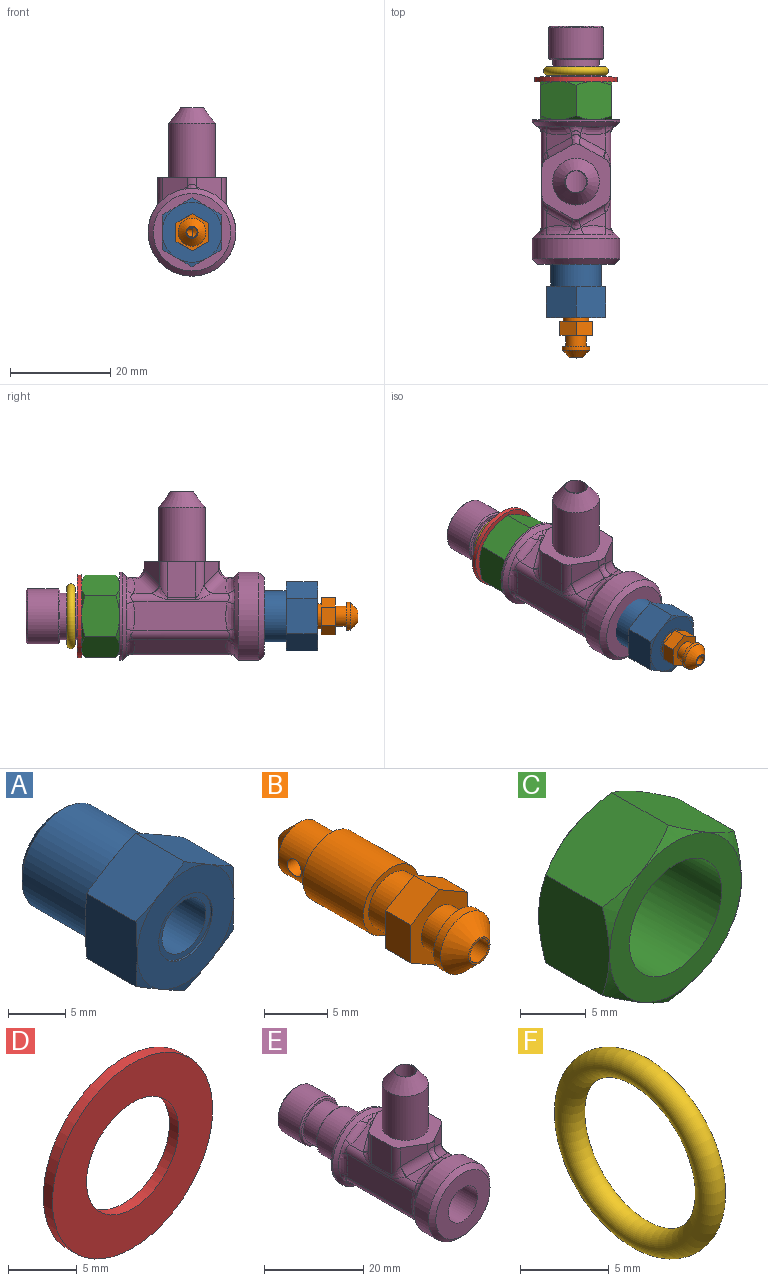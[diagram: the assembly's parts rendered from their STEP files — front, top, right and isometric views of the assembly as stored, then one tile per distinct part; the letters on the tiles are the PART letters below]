
ASSEMBLY  parts=6 mates=5
PART A: 29 faces, bbox 14.3x16.2x14.3 mm
  f0: cylinder r=2.71mm len=12.32mm, axis (0,-1,0), area 209.4mm2, adj f1,f26
  f1: cone r=0mm half-angle=59deg, axis (0,-1,0), area 21.7mm2, adj f0,f24
  f2: cylinder r=5.08mm len=10.16mm, axis (0,-1,0), area 278.1mm2, adj f4,f28
  f3: plane 8.89x8.89mm, normal (0,1,0), area 57.3mm2, adj f27,f28
  f4: plane 11.94x11.94mm, normal (0,1,0), area 30.9mm2, adj f2,f5,f6,f7,f8,f9,f10
  f5: cone r=6.89mm half-angle=82.2deg, axis (0,-1,0), area 3.1mm2, adj f4,f11,f16
  f6: cone r=6.89mm half-angle=82.2deg, axis (0,-1,0), area 3.1mm2, adj f4,f11,f12
  f7: cone r=6.89mm half-angle=82.2deg, axis (0,-1,0), area 3.1mm2, adj f4,f12,f13
  f8: cone r=6.89mm half-angle=82.2deg, axis (0,-1,0), area 3.1mm2, adj f4,f13,f14
  f9: cone r=6.89mm half-angle=82.2deg, axis (0,-1,0), area 3.1mm2, adj f4,f14,f15
  f10: cone r=6.89mm half-angle=82.2deg, axis (0,-1,0), area 3.1mm2, adj f4,f15,f16
  f11: plane 6.85x6.47mm, normal (0.5,0,-0.87), area 43.2mm2, adj f5,f6,f12,f16,f17,f18
  f12: plane 6.85x6.47mm, normal (-0.5,0,-0.87), area 43.2mm2, adj f6,f7,f11,f13,f18,f19
  f13: plane 7.4x6.86mm, normal (-1,0,0), area 43.2mm2, adj f7,f8,f12,f14,f19,f20
  f14: plane 6.85x6.47mm, normal (-0.5,0,0.87), area 43.2mm2, adj f8,f9,f13,f15,f20,f21
  f15: plane 6.85x6.47mm, normal (0.5,0,0.87), area 43.2mm2, adj f9,f10,f14,f16,f21,f22
  f16: plane 7.4x6.86mm, normal (1,0,0), area 43.2mm2, adj f5,f10,f11,f15,f17,f22
  f17: cone r=6.89mm half-angle=82.2deg, axis (0,1,0), area 3.1mm2, adj f11,f16,f23
  f18: cone r=6.89mm half-angle=82.2deg, axis (0,1,0), area 3.1mm2, adj f11,f12,f23
  f19: cone r=6.89mm half-angle=82.2deg, axis (0,1,0), area 3.1mm2, adj f12,f13,f23
  f20: cone r=6.89mm half-angle=82.2deg, axis (0,1,0), area 3.1mm2, adj f13,f14,f23
  f21: cone r=6.89mm half-angle=82.2deg, axis (0,1,0), area 3.1mm2, adj f14,f15,f23
  f22: cone r=6.89mm half-angle=82.2deg, axis (0,1,0), area 3.1mm2, adj f15,f16,f23
  f23: plane 11.94x11.94mm, normal (0,-1,0), area 77.7mm2, adj f17,f18,f19,f20,f21,f22,f25
  f24: cylinder r=1.19mm len=2.38mm, axis (0,-1,0), area 16.5mm2, adj f1,f27
  f25: cylinder r=3.3mm len=6.6mm, axis (0,-1,0), area 4.2mm2, adj f23,f26
  f26: plane 6.6x6.6mm, normal (0,-1,0), area 11.3mm2, adj f0,f25
  f27: cone r=1.19mm half-angle=45deg, axis (0,1,0), area 0.5mm2, adj f3,f24
  f28: cone r=5.08mm half-angle=45deg, axis (0,-1,0), area 26.9mm2, adj f2,f3
PART B: 24 faces, bbox 6.4x21.8x7.4 mm
  f0: cylinder r=2.39mm len=4.78mm, axis (0,-1,0), area 51mm2, adj f6,f16,f23
  f1: cone r=0mm half-angle=59deg, axis (0,-1,0), area 2.2mm2, adj f2,f22,f23
  f2: cylinder r=1.04mm len=18.39mm, axis (0,-1,0), area 119.2mm2, adj f1,f19,f23
  f3: cylinder r=2.53mm len=5.05mm, axis (0,-1,0), area 40.3mm2, adj f7,f14
  f4: cylinder r=3.14mm len=6.78mm, axis (0,-1,0), area 133.7mm2, adj f6,f7
  f5: plane 1.47x1.47mm, normal (0,1,0), area 1.7mm2, adj f16
  f6: plane 6.27x6.27mm, normal (0,1,0), area 13mm2, adj f0,f4
  f7: plane 6.27x6.27mm, normal (0,-1,0), area 10.8mm2, adj f3,f4
  f8: plane 3.68x2.84mm, normal (1,0,0), area 10.5mm2, adj f9,f13,f14,f15
  f9: plane 3.19x2.84mm, normal (0.5,0,0.87), area 10.5mm2, adj f8,f10,f14,f15
  f10: plane 3.19x2.84mm, normal (-0.5,0,0.87), area 10.5mm2, adj f9,f11,f14,f15
  f11: plane 3.68x2.84mm, normal (-1,0,0), area 10.5mm2, adj f10,f12,f14,f15
  f12: plane 3.19x2.84mm, normal (-0.5,0,-0.87), area 10.5mm2, adj f11,f13,f14,f15
  f13: plane 3.19x2.84mm, normal (0.5,0,-0.87), area 10.5mm2, adj f8,f12,f14,f15
  f14: plane 7.36x6.38mm, normal (0,1,0), area 15.1mm2, adj f3,f8,f9,f10,f11,f12,f13
  f15: plane 7.36x6.38mm, normal (0,-1,0), area 22.6mm2, adj f8,f9,f10,f11,f12,f13,f17
  f16: cone r=2.39mm half-angle=45deg, axis (0,-1,0), area 22.9mm2, adj f0,f5
  f17: cylinder r=2.01mm len=4.01mm, axis (0,1,0), area 27.2mm2, adj f15,f18
  f18: plane 5.56x5.56mm, normal (0,1,0), area 11.7mm2, adj f17,f20
  f19: plane 2.41x2.41mm, normal (0,-1,0), area 1.2mm2, adj f2,f21
  f20: cylinder r=2.78mm len=5.56mm, axis (0,1,0), area 13.3mm2, adj f18,f21
  f21: cone r=1.21mm half-angle=45deg, axis (0,1,0), area 27.9mm2, adj f19,f20
  f22: plane 1.56x0.64mm, normal (-1,0,0), area 0.4mm2, adj f1,f23
  f23: cylinder r=0.79mm len=2.39mm, axis (1,0,0), area 9.3mm2, adj f0,f1,f2,f22
PART C: 11 faces, bbox 16.4x7.6x16.4 mm
  f0: plane 14.2x14.2mm, normal (0,1,0), area 81mm2, adj f1,f10
  f1: cone r=8.21mm half-angle=55.2deg, axis (0,-1,0), area 20.6mm2, adj f0,f2,f3,f4,f5,f6,f7
  f2: plane 8.22x7.63mm, normal (1,0,0), area 58.3mm2, adj f1,f3,f7,f8
  f3: plane 7.64x7.11mm, normal (0.5,0,0.87), area 58.3mm2, adj f1,f2,f4,f8
  f4: plane 7.64x7.11mm, normal (-0.5,0,0.87), area 58.3mm2, adj f1,f3,f5,f8
  f5: plane 8.22x7.63mm, normal (-1,0,0), area 58.3mm2, adj f1,f4,f6,f8
  f6: plane 7.64x7.11mm, normal (-0.5,0,-0.87), area 58.3mm2, adj f1,f5,f7,f8
  f7: plane 7.64x7.11mm, normal (0.5,0,-0.87), area 58.3mm2, adj f1,f2,f6,f8
  f8: cone r=7.09mm half-angle=54.8deg, axis (0,1,0), area 20.9mm2, adj f2,f3,f4,f5,f6,f7,f9
  f9: plane 14.19x14.19mm, normal (0,-1,0), area 80.8mm2, adj f8,f10
  f10: cylinder r=4.96mm len=9.92mm, axis (0,1,0), area 238.3mm2, adj f0,f9
PART D: 4 faces, bbox 16.5x0.9x16.5 mm
  f0: cylinder r=4.75mm len=9.5mm, axis (0,1,0), area 28mm2, adj f2,f3
  f1: cylinder r=8.27mm len=16.54mm, axis (0,1,0), area 48.8mm2, adj f2,f3
  f2: plane 16.54x16.54mm, normal (0,-1,0), area 143.9mm2, adj f0,f1
  f3: plane 16.54x16.54mm, normal (0,1,0), area 143.9mm2, adj f0,f1
PART E: 97 faces, bbox 17.5x47.4x33.5 mm
  f0: cone r=0mm half-angle=59deg, axis (0,-1,0), area 45mm2, adj f1,f91
  f1: cylinder r=4.13mm len=21.11mm, axis (0,-1,0), area 532.3mm2, adj f0,f9,f80,f81,f82
  f2: plane 4.99x3.7mm, normal (0.5,0,0.87), area 11.6mm2, adj f7,f19,f47,f70,f72
  f3: plane 4.99x3.06mm, normal (0.5,0,0.87), area 7.9mm2, adj f6,f19,f27,f61,f62
  f4: plane 4.99x3.7mm, normal (-0.5,0,0.87), area 11.6mm2, adj f7,f23,f43,f75,f76
  f5: plane 4.99x3.06mm, normal (-0.5,0,0.87), area 7.9mm2, adj f6,f23,f24,f65,f67
  f6: cylinder r=1.91mm len=1.91mm, axis (0,1,0), area 0.2mm2, adj f3,f5,f25,f63
  f7: cylinder r=1.91mm len=1.91mm, axis (0,1,0), area 1.5mm2, adj f2,f4,f45,f74
  f8: cylinder r=8.74mm len=17.48mm, axis (0,1,0), area 225.2mm2, adj f16,f18
  f9: plane 15.42x15.42mm, normal (0,-1,0), area 133.2mm2, adj f1,f18
  f10: plane 18.84x5.77mm, normal (1,0,0), area 105.8mm2, adj f19,f20,f31,f44
  f11: plane 18.84x4.99mm, normal (0.5,0,-0.87), area 105.8mm2, adj f20,f21,f35,f40
  f12: plane 18.84x4.99mm, normal (-0.5,0,-0.87), area 105.8mm2, adj f21,f22,f32,f36
  f13: plane 18.84x5.77mm, normal (-1,0,0), area 105.8mm2, adj f22,f23,f28,f39
  f14: plane 17.48x17.48mm, normal (0,1,0), area 172.3mm2, adj f15,f83
  f15: cylinder r=8.74mm len=17.48mm, axis (0,1,0), area 24.4mm2, adj f14,f17
  f16: cone r=8.74mm half-angle=45deg, axis (0,-1,0), area 61.1mm2, adj f8,f24,f25,f26,f27,f28,f29,f30
  f17: cone r=7.91mm half-angle=45deg, axis (0,1,0), area 61.1mm2, adj f15,f36,f37,f38,f39,f40,f41,f42
  f18: cone r=7.71mm half-angle=45deg, axis (0,1,0), area 75.2mm2, adj f8,f9
  f19: cylinder r=1.91mm len=19.66mm, axis (0,1,0), area 23.9mm2, adj f2,f3,f10,f29,f46,f64,f66,f68
  f20: cylinder r=1.91mm len=19.66mm, axis (0,1,0), area 38.6mm2, adj f10,f11,f33,f42
  f21: cylinder r=1.91mm len=19.66mm, axis (0,1,0), area 38.6mm2, adj f11,f12,f34,f38
  f22: cylinder r=1.91mm len=19.66mm, axis (0,1,0), area 38.6mm2, adj f12,f13,f30,f37
  f23: cylinder r=1.91mm len=19.66mm, axis (0,1,0), area 23.9mm2, adj f4,f5,f13,f26,f41,f69,f71,f73
  f24: bspline ~5.5x3.41mm, area 10.1mm2, adj f5,f16,f25,f26
  f25: bspline ~3.92x1.51mm, area 3.1mm2, adj f6,f16,f24,f27
  f26: bspline ~3.43x2.14mm, area 3.1mm2, adj f16,f23,f24,f28
  f27: bspline ~4.99x3.21mm, area 10.1mm2, adj f3,f16,f25,f29
  f28: bspline ~6.35x1.69mm, area 10.1mm2, adj f13,f16,f26,f30
  f29: bspline ~3.43x2.14mm, area 3.1mm2, adj f16,f19,f27,f31
  f30: bspline ~3.43x2.14mm, area 3.1mm2, adj f16,f22,f28,f32
  f31: bspline ~6.35x1.69mm, area 10.1mm2, adj f10,f16,f29,f33
  f32: bspline ~4.99x3.21mm, area 10.1mm2, adj f12,f16,f30,f34
  f33: bspline ~3.43x2.14mm, area 3.1mm2, adj f16,f20,f31,f35
  f34: bspline ~3.92x1.51mm, area 3.1mm2, adj f16,f21,f32,f35
  f35: bspline ~5.5x3.41mm, area 10.1mm2, adj f11,f16,f33,f34
  f36: bspline ~4.99x3.21mm, area 10.1mm2, adj f12,f17,f37,f38
  f37: bspline ~3.43x2.14mm, area 3.1mm2, adj f17,f22,f36,f39
  f38: bspline ~3.92x1.51mm, area 3.1mm2, adj f17,f21,f36,f40
  f39: bspline ~6.35x1.69mm, area 10.1mm2, adj f13,f17,f37,f41
  f40: bspline ~5.5x3.41mm, area 10.1mm2, adj f11,f17,f38,f42
  f41: bspline ~3.43x2.14mm, area 3.1mm2, adj f17,f23,f39,f43
  f42: bspline ~3.43x2.14mm, area 3.1mm2, adj f17,f20,f40,f44
  f43: bspline ~5.5x3.41mm, area 10.1mm2, adj f4,f17,f41,f45
  f44: bspline ~6.35x1.69mm, area 10.1mm2, adj f10,f17,f42,f46
  f45: bspline ~3.92x1.51mm, area 3.1mm2, adj f7,f17,f43,f47
  f46: bspline ~3.43x2.14mm, area 3.1mm2, adj f17,f19,f44,f47
  f47: bspline ~4.99x3.21mm, area 10.1mm2, adj f2,f17,f45,f46
  f48: plane 7.03x5.63mm, normal (1,0,0), area 39.5mm2, adj f54,f55,f60,f66
  f49: plane 4.87x4.61mm, normal (0.5,0.87,0), area 18mm2, adj f54,f55,f56,f72
  f50: plane 4.87x4.61mm, normal (-0.5,0.87,0), area 18mm2, adj f54,f56,f57,f76
  f51: plane 7.03x5.63mm, normal (-1,0,0), area 39.5mm2, adj f54,f57,f58,f71
  f52: plane 4.87x4.61mm, normal (-0.5,-0.87,0), area 18mm2, adj f54,f58,f59,f65
  f53: plane 4.87x4.61mm, normal (0.5,-0.87,0), area 18mm2, adj f54,f59,f60,f61
  f54: plane 15.06x13.55mm, normal (0,0,1), area 90.4mm2, adj f48,f49,f50,f51,f52,f53,f55,f56
  f55: cylinder r=1.91mm len=7.03mm, axis (0,0,-1), area 11.7mm2, adj f48,f49,f54,f68,f70
  f56: cylinder r=1.91mm len=1.91mm, axis (0,0,-1), area 2.9mm2, adj f49,f50,f54,f74
  f57: cylinder r=1.91mm len=7.03mm, axis (0,0,-1), area 11.7mm2, adj f50,f51,f54,f73,f75
  f58: cylinder r=1.91mm len=7.03mm, axis (0,0,-1), area 11.7mm2, adj f51,f52,f54,f67,f69
  f59: cylinder r=1.91mm len=1.91mm, axis (0,0,-1), area 2.9mm2, adj f52,f53,f54,f63
  f60: cylinder r=1.91mm len=7.03mm, axis (0,0,-1), area 11.7mm2, adj f48,f53,f54,f62,f64
  f61: cylinder r=1.91mm len=5.12mm, axis (-0.77,-0.45,0.45), area 15.8mm2, adj f3,f53,f62,f63
  f62: bspline ~2.31x2.12mm, area 0.3mm2, adj f3,f60,f61,f64
  f63: bspline ~2.26x2.26mm, area 5mm2, adj f6,f59,f61,f65
  f64: bspline ~3.78x3.1mm, area 4.3mm2, adj f19,f60,f62,f66
  f65: cylinder r=1.91mm len=5.12mm, axis (-0.77,0.45,-0.45), area 15.8mm2, adj f5,f52,f63,f67
  f66: cylinder r=1.91mm len=5.63mm, axis (0,1,0), area 2.7mm2, adj f19,f48,f64,f68
  f67: bspline ~2.31x2.12mm, area 0.3mm2, adj f5,f58,f65,f69
  f68: bspline ~3.38x2.9mm, area 4.3mm2, adj f19,f55,f66,f70
  f69: bspline ~3.38x2.9mm, area 4.3mm2, adj f23,f58,f67,f71
  f70: bspline ~2.31x2.12mm, area 0.3mm2, adj f2,f55,f68,f72
  f71: cylinder r=1.91mm len=5.63mm, axis (0,1,0), area 2.7mm2, adj f23,f51,f69,f73
  f72: cylinder r=1.91mm len=5.12mm, axis (0.77,-0.45,-0.45), area 15.8mm2, adj f2,f49,f70,f74
  f73: bspline ~3.59x3.1mm, area 4.3mm2, adj f23,f57,f71,f75
  f74: bspline ~2.26x2.26mm, area 5mm2, adj f7,f56,f72,f76
  f75: bspline ~2.31x2.12mm, area 0.3mm2, adj f4,f57,f73,f76
  f76: cylinder r=1.91mm len=5.12mm, axis (0.77,0.45,0.45), area 15.8mm2, adj f4,f50,f74,f75
  f77: cylinder r=4.64mm len=10.82mm, axis (0,0,-1), area 315.2mm2, adj f54,f79
  f78: plane 4.52x4.52mm, normal (0,0,1), area 1mm2, adj f79,f82
  f79: cone r=2.26mm half-angle=37.5deg, axis (0,0,-1), area 84.6mm2, adj f77,f78
  f80: cone r=0mm half-angle=59deg, axis (0,0,1), area 0.2mm2, adj f1,f82
  f81: cone r=0mm half-angle=59deg, axis (0,0,1), area 0.2mm2, adj f1,f82
  f82: cylinder r=2.18mm len=21.11mm, axis (0,0,1), area 287.1mm2, adj f1,f78,f80,f81
  f83: cylinder r=4.64mm len=9.27mm, axis (0,-1,0), area 44.4mm2, adj f14,f84
  f84: plane 10.36x10.36mm, normal (0,-1,0), area 16.8mm2, adj f83,f92
  f85: cylinder r=5.49mm len=10.97mm, axis (0,-1,0), area 190mm2, adj f92,f93
  f86: cylinder r=4.64mm len=9.27mm, axis (0,-1,0), area 125mm2, adj f87,f88
  f87: plane 10.36x10.36mm, normal (0,-1,0), area 16.8mm2, adj f86,f94
  f88: plane 10.36x10.36mm, normal (0,1,0), area 16.8mm2, adj f86,f93
  f89: plane 10.36x10.36mm, normal (0,1,0), area 64.9mm2, adj f95,f96
  f90: cylinder r=5.49mm len=10.97mm, axis (0,-1,0), area 211mm2, adj f94,f95
  f91: cylinder r=2.18mm len=24.84mm, axis (0,1,0), area 341mm2, adj f0,f96
  f92: cone r=5.18mm half-angle=45deg, axis (0,1,0), area 14.4mm2, adj f84,f85
  f93: cone r=5.49mm half-angle=45deg, axis (0,-1,0), area 14.4mm2, adj f85,f88
  f94: cone r=5.18mm half-angle=45deg, axis (0,1,0), area 14.4mm2, adj f87,f90
  f95: cone r=5.49mm half-angle=45deg, axis (0,-1,0), area 14.4mm2, adj f89,f90
  f96: cone r=2.18mm half-angle=45deg, axis (0,1,0), area 6.3mm2, adj f89,f91
PART F: 1 faces, bbox 1.7x14x14 mm
  f0: torus R=5.6mm, axis (-1,0,0), area 188.1mm2
PLACE A t=(5.69,-22.51,41.4)mm
PLACE B t=(5.69,-25.99,41.4)mm
PLACE C t=(5.69,24.59,41.4)mm
PLACE D t=(5.69,25.46,41.4)mm
PLACE E t=(5.69,16.94,41.4)mm
PLACE F rot(axis=(0,0,1),90deg) t=(5.69,26.67,41.4)mm
MATE cylindrical B.f4 <-> A.f0  axis (0,-1,0) through (5.69,-20.61,41.4)mm
MATE cylindrical D.f0 <-> C.f1  axis (0,-1,0) through (5.69,24.52,41.4)mm
MATE fastened A.f2 <-> E.f0  axis (0,-1,0) through (5.69,-11.81,41.4)mm
MATE revolute C.f1 <-> E.f83  axis (0,1,0) through (5.69,16.94,41.4)mm
MATE cylindrical F.f0 <-> E.f83  axis (0,-1,0) through (5.69,26.67,41.4)mm
